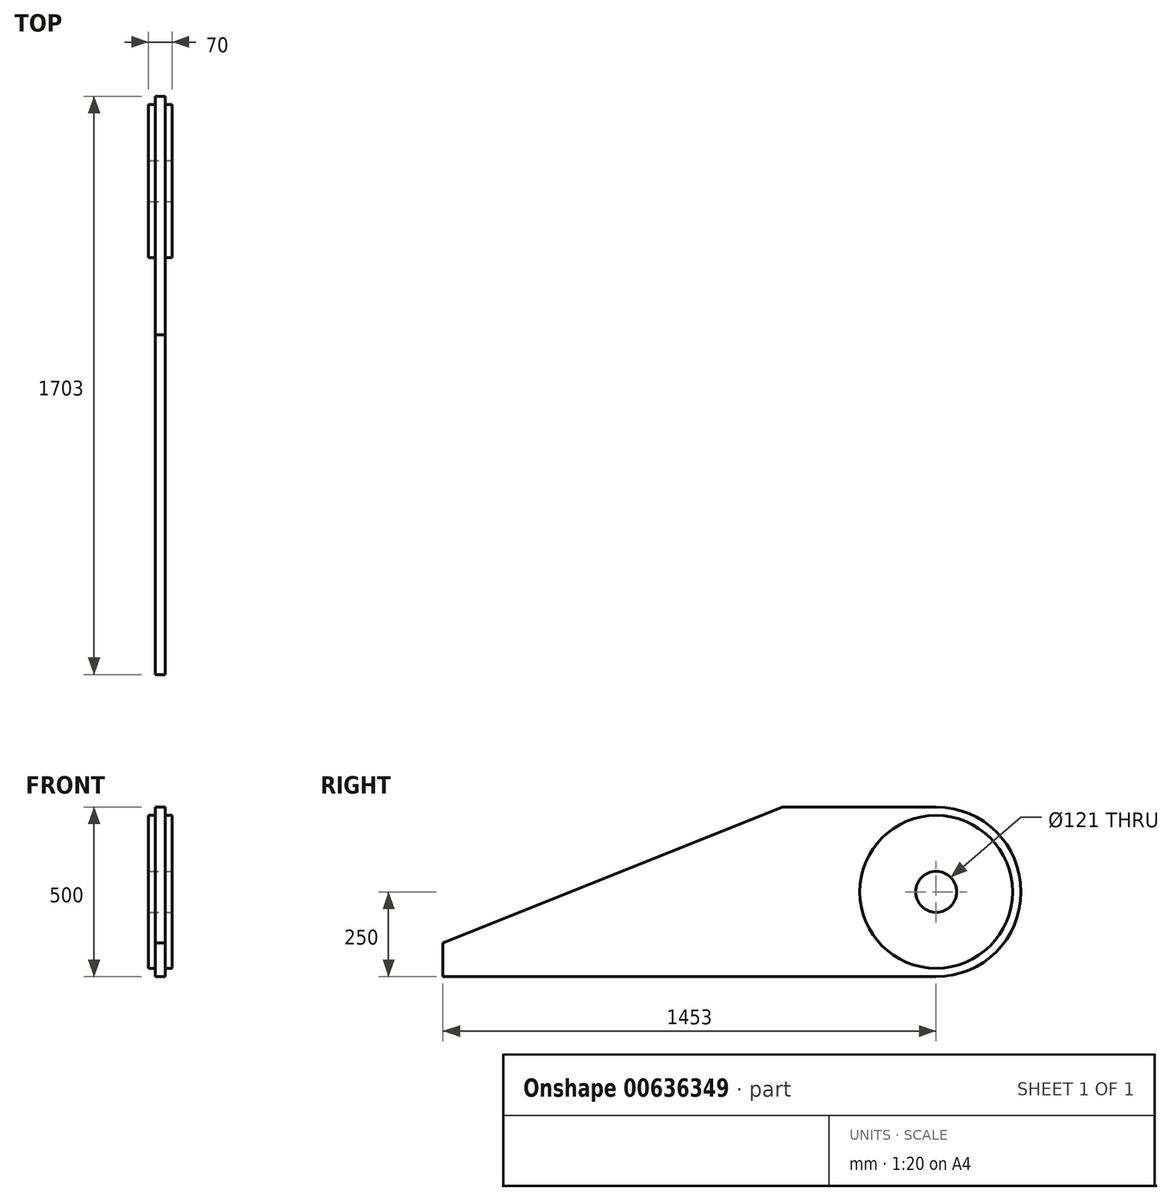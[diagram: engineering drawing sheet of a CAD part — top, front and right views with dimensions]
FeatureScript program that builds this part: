
annotation { "Feature Type Name" : "Feature", "Feature Type Description" : "" }
export const myFeature = defineFeature(function(context is Context, id is Id, definition is map)
    precondition{}
    {
        {
            var Q0;
            Q0=qCreatedBy(makeId("Right.planeOp"),FACE);
            var sketch = newSketch(context, id + "F0", { "sketchPlane" : qUnion([Q0])});
            skLineSegment(sketch, "E0", {"start": v(-726.5, 0) * mm, "end": v(726.5, 0) * mm});
            skLineSegment(sketch, "E1", {"start": v(-726.5, 0) * mm, "end": v(-726.5, 100) * mm});
            skLineSegment(sketch, "E2", {"start": v(-726.5, 100) * mm, "end": v(273.5, 500) * mm});
            skLineSegment(sketch, "E3", {"start": v(273.5, 500) * mm, "end": v(726.5, 500) * mm});
            skPoint(sketch, "E4", {"position": v(726.5, 250) * mm});
            skArc(sketch, "E5", {"start": v(726.5, 0) * mm, "mid": v(976.5, 250) * mm, "end": v(726.5, 500) * mm});
            skCircle(sketch, "E6", {"center": v(726.5, 250) * mm, "radius": 60.5 * mm});
            skCircle(sketch, "E7", {"center": v(726.5, 250) * mm, "radius": 225 * mm});
            skSolve(sketch);
        }
        {
            var Q0;
            Q0=makeQuery(id+"F0.imprint","IMPRINT",FACE,{"disambiguationData":[TD([[makeQuery(id+"F0.imprint","IMPRINT",EDGE,{"derivedFrom":sQuery(id+"F0.wireOp",EDGE,"E0")}),1.0]])]});
            var Q1;
            Q1=makeQuery(id+"F0.imprint","IMPRINT",FACE,{"disambiguationData":[TD([[makeQuery(id+"F0.imprint","IMPRINT",EDGE,{"derivedFrom":sQuery(id+"F0.wireOp",EDGE,"E6")}),-1.0]])]});
            extrude(context, id + "F1", {"entities" : qUnion([Q0, Q1]), "endBound" : BoundingType.SYMMETRIC, "oppositeDirection" : true, "depth" : 30 * mm, "offsetDistance" : 25 * mm});
        }
        {
            var Q0;
            Q0=makeQuery(id+"F1.opExtrude","CAP_FACE",FACE,{"disambiguationData":[OSD([sQuery(id+"F0.wireOp",EDGE,"E0"),sQuery(id+"F0.wireOp",EDGE,"E1"),sQuery(id+"F0.wireOp",EDGE,"E2"),sQuery(id+"F0.wireOp",EDGE,"E3"),sQuery(id+"F0.wireOp",EDGE,"E5"),sQuery(id+"F0.wireOp",EDGE,"E6")])],"isStart":false});
            var sketch = newSketch(context, id + "F2", { "sketchPlane" : qUnion([Q0])});
            skCircle(sketch, "E8.0", {"center": v(-726.5, 250) * mm, "radius": 225 * mm});
            skCircle(sketch, "E9.0", {"center": v(-726.5, 250) * mm, "radius": 60.5 * mm});
            skCircle(sketch, "E9.1", {"center": v(-726.5, 250) * mm, "radius": 60.5 * mm});
            skSolve(sketch);
        }
        {
            var Q0;
            Q0 = qSketchRegion(id + "F2", true);
            extrude(context, id + "F3", {"entities" : qUnion([Q0]), "depth" : 20 * mm, "offsetDistance" : 25 * mm});
        }
        {
            var Q0;
            Q0=makeQuery(id+"F3.opExtrude","SWEPT_BODY",BODY,{"disambiguationData":[OSD([sQuery(id+"F2.wireOp",EDGE,"E8.0"),sQuery(id+"F2.wireOp",EDGE,"E9.1")])]});
            var Q1;
            Q1=qCreatedBy(makeId("Right.planeOp"),FACE);
            mirror(context, id + "F4", {"operationType" : NewBodyOperationType.ADD, "entities" : qUnion([Q0]), "mirrorPlane" : qUnion([Q1])});
        }
    });
